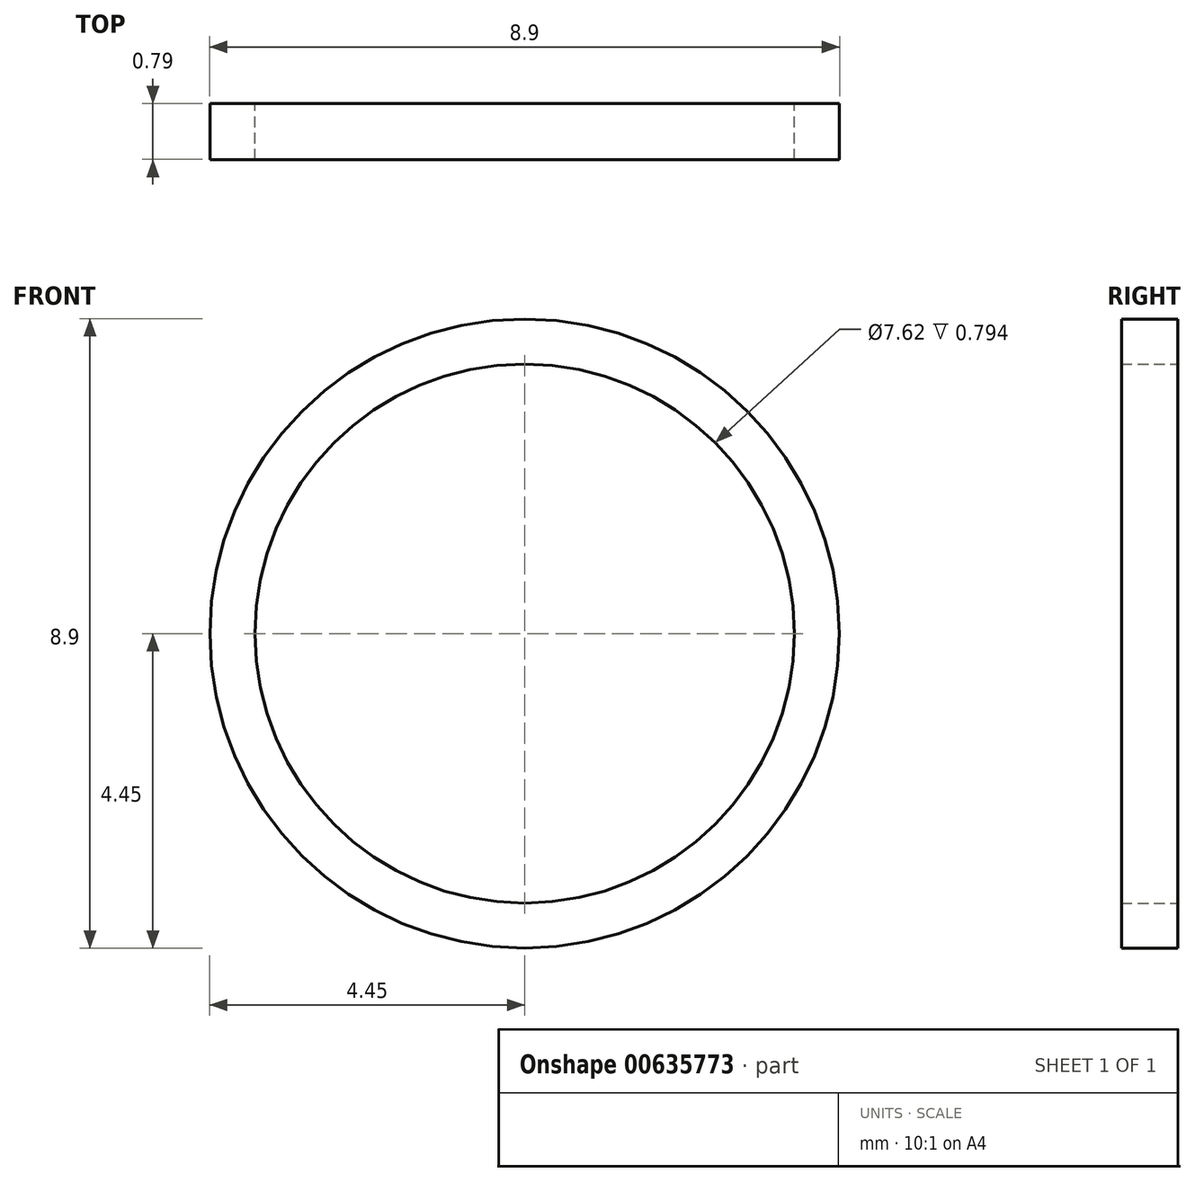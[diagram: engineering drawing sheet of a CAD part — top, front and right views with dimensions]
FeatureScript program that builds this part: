
annotation { "Feature Type Name" : "Feature", "Feature Type Description" : "" }
export const myFeature = defineFeature(function(context is Context, id is Id, definition is map)
    precondition{}
    {
        {
            var Q0;
            Q0=qCreatedBy(makeId("Front.planeOp"),FACE);
            var sketch = newSketch(context, id + "F0", { "sketchPlane" : qUnion([Q0])});
            skCircle(sketch, "E0", {"center": v(0, 0) * mm, "radius": 3.81 * mm});
            skCircle(sketch, "E1", {"center": v(0, 0) * mm, "radius": 4.45 * mm});
            skSolve(sketch);
        }
        {
            var Q0;
            Q0 = qSketchRegion(id + "F0", true);
            extrude(context, id + "F1", {"entities" : qUnion([Q0]), "depth" : 0.8 * mm, "offsetDistance" : 25.4 * mm});
        }
    });
